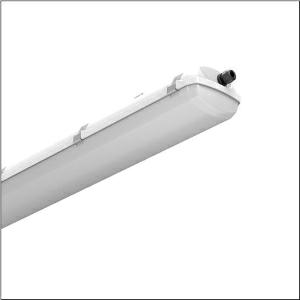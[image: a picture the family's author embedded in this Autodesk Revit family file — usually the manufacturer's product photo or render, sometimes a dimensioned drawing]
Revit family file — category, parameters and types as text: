
# Revit family: monsun_r__ex_51fxb1dp670a_cf6b
name_source: partatom
category: Lighting Fixtures
units: mm (PartAtom-declared; Revit-internal decimal feet)

## family parameters
Cut with Voids When Loaded = No
Host = Face
Light Source = No
Part Type = Normal
Room Calculation Point = No
Round Connector Dimension = Use Diameter
Shared = No

## types (1)
- Monsun® Ex (1 x LED, 7310 lm, 43.8 W, 6500K)
    Apparent Load = 44 VA
    CIE Flux Codes = 61 86 97 100 100
    Color Rendering = 80
    Color Temperature = 6500K
    Default Elevation = 1800 mm
    Description = Monsun® Ex, damp-proof luminaire, primary optical cover: cover, of PC, UV-stabilised, opal, light emission: direct distribution, primary light characteristic: symmetric, installation type: surface-mounted, LED, rated luminous flux: 7.310lm, luminous efficacy: 167lm/W, light colour: 865, colour temperature: 6500K, control gear: ECG DALI, with terminal, 5-pole, max. 2.5mm², through-wiring: 7x 2.5mm², mains connection: 220..240V, AC, 50/60Hz, rated input power: 44W, housing, of PC, light grey (RAL 7035), incl. blind plug, incl. 1x Ex cable gland M20 for cable diameter 7..12mm with sealing, length: 1.580mm, width: 155mm, height: 105mm, clip for enclosure, of stainless steel, protection rating (complete): IP66, insulation class (complete): insulation class I (protective earthing), certification: CE, explosion class: zone2,22 II 3G Ex nR IIC T6 GC, II 3D Ex tc IIIC T80°C Dc, impact resistance: IK10, permissible operating ambient temperature: -20..+60°C, LABS conformity tested according to VDMA 24364:2018-05, contact your sales advisor before using the luminaires in applications with unclear chemical exposure, large temperature fluctuations or condensation-forming humidity, packaging unit: 1 piece
    Height = 105 mm
    Lamp = 1 x LED
    Lamp Light Flux = 7310 lm
    Lamp Power = 43.8 W
    Lamp count = 1
    Length = 1580 mm
    Luminous efficacy = 167 lm/W
    Manufacturer = Siteco
    ModVariant = No
    Model = 51FXB1DP670A
    Mounting Place = Ceiling
    Mounting Type = Surface mounted
    Number of Poles = 1
    OnlyDefault = Yes
    Power Factor = 1
    Product Name = Monsun® Ex
    Product group = damp-proof luminaire
    ProductGroupID = 301
    Protection Class = Protection class I
    Protection Degree = IP 66
    RLX_Detail_Level = 1
    RLX_Emergency_Light_Flux = 0 lm
    RLX_Emergency_Type = 0
    RLX_Emergency_Type_DB = No
    RlxData = <blob elided: 41637 chars, md5=ac885bc8>
    Socket = socket
    Standby Power = 0 W
    System Light Flux = 7310 lm
    System Power = 44 W
    Type Comments = Product without accessories
    Type Image = l_1258882.jpg
    URL = http://relux.com
    VarID = ---
    Voltage = 0 V
    Weight = 0.00 kg
    Width = 155 mm

## geometry (parser evidence)
native form markers: Blend x4, Sweep x8
no freeform markers — native parametric forms only
